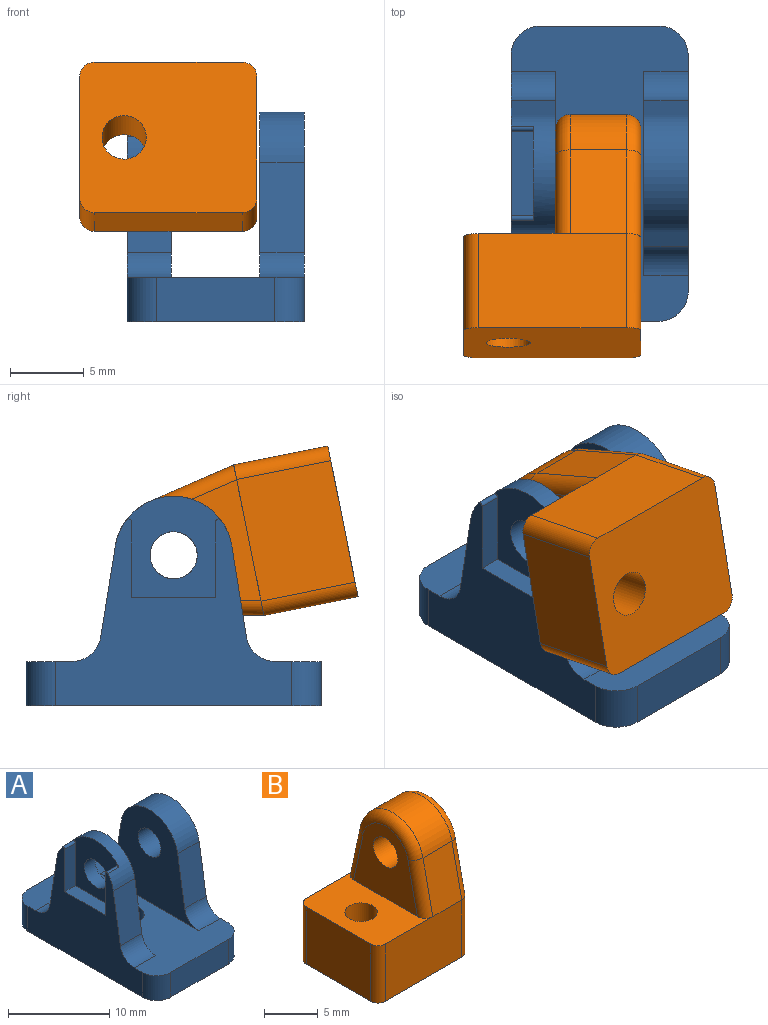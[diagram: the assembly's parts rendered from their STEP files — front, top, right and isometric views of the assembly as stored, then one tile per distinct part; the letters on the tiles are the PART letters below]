
ASSEMBLY  parts=2 mates=1
PART A: 31 faces, bbox 12x20x14.2 mm
  f0: cylinder r=4mm len=7.9mm, axis (-1,0,0), area 22.7mm2, adj f4,f14,f15,f16,f28,f29,f30
  f1: cylinder r=1.6mm len=3.2mm, axis (-1,0,0), area 15.1mm2, adj f16,f28
  f2: plane 16x14.2mm, normal (1,0,0), area 132.9mm2, adj f7,f8,f9,f10,f11,f12,f19,f20
  f3: plane 8x3mm, normal (0,1,0), area 24mm2, adj f7,f8,f21,f22
  f4: plane 16x12.67mm, normal (-1,0,0), area 103.9mm2, adj f0,f7,f8,f14,f15,f17,f18,f22
  f5: plane 8x3mm, normal (0,-1,0), area 24mm2, adj f7,f8,f23,f24
  f6: cylinder r=1.6mm len=3.2mm, axis (0,0,-1), area 30.2mm2, adj f7,f8
  f7: plane 20x12mm, normal (0,0,1), area 145.7mm2, adj f2,f3,f4,f5,f6,f13,f16,f17
  f8: plane 20x12mm, normal (0,0,-1), area 228.5mm2, adj f2,f3,f4,f5,f6,f21,f22,f23
  f9: cylinder r=4mm len=7.9mm, axis (1,0,0), area 33.9mm2, adj f2,f10,f12,f13
  f10: plane 6.15x3mm, normal (0,-0.99,0.16), area 18.7mm2, adj f2,f9,f13,f19
  f11: cylinder r=1.6mm len=3.2mm, axis (1,0,0), area 30.2mm2, adj f2,f13
  f12: plane 6.15x3mm, normal (0,0.99,0.16), area 18.7mm2, adj f2,f9,f13,f20
  f13: plane 13.81x11.2mm, normal (-1,0,0), area 84.9mm2, adj f7,f9,f10,f11,f12,f19,f20
  f14: plane 6.15x3mm, normal (0,0.99,0.16), area 18.7mm2, adj f0,f4,f16,f18
  f15: plane 6.15x3mm, normal (0,-0.99,0.16), area 18.7mm2, adj f0,f4,f16,f17
  f16: plane 13.81x11.2mm, normal (1,0,0), area 84.9mm2, adj f0,f1,f7,f14,f15,f17,f18
  f17: cylinder r=2mm len=3mm, axis (-1,0,0), area 8.5mm2, adj f4,f7,f15,f16
  f18: cylinder r=2mm len=3mm, axis (-1,0,0), area 8.5mm2, adj f4,f7,f14,f16
  f19: cylinder r=2mm len=3mm, axis (-1,0,0), area 8.5mm2, adj f2,f7,f10,f13
  f20: cylinder r=2mm len=3mm, axis (-1,0,0), area 8.5mm2, adj f2,f7,f12,f13
  f21: cylinder r=2mm len=3mm, axis (0,0,1), area 9.4mm2, adj f2,f3,f7,f8
  f22: cylinder r=2mm len=3mm, axis (0,0,-1), area 9.4mm2, adj f3,f4,f7,f8
  f23: cylinder r=2mm len=3mm, axis (0,0,1), area 9.4mm2, adj f4,f5,f7,f8
  f24: cylinder r=2mm len=3mm, axis (0,0,-1), area 9.4mm2, adj f2,f5,f7,f8
  f25: plane 5.12x1.5mm, normal (0,-1,0), area 7.7mm2, adj f4,f26,f28,f29
  f26: plane 5.7x1.5mm, normal (0,0,1), area 8.6mm2, adj f4,f25,f27,f28
  f27: plane 5.12x1.5mm, normal (0,1,0), area 7.7mm2, adj f4,f26,f28,f30
  f28: plane 6.85x6.42mm, normal (-1,0,0), area 29mm2, adj f0,f1,f25,f26,f27,f29,f30
  f29: cylinder r=0.2mm len=1.5mm, axis (-1,0,0), area 0.8mm2, adj f0,f4,f25,f28
  f30: cylinder r=0.2mm len=1.5mm, axis (-1,0,0), area 0.8mm2, adj f0,f4,f27,f28
PART B: 22 faces, bbox 12x10.4x16 mm
  f0: plane 14.7x8.4mm, normal (1,0,0), area 98.4mm2, adj f6,f9,f12,f13,f14,f15,f16
  f1: plane 10x6.5mm, normal (0,1,0), area 65mm2, adj f5,f6,f10,f12,f20
  f2: plane 8.4x6.5mm, normal (-1,0,0), area 54.6mm2, adj f5,f6,f20,f21
  f3: plane 10x6.5mm, normal (0,-1,0), area 65mm2, adj f5,f6,f8,f15,f21
  f4: cylinder r=1.5mm len=6.5mm, axis (0,0,-1), area 61.3mm2, adj f5,f6
  f5: plane 10.4x7.2mm, normal (0,0,1), area 57.4mm2, adj f1,f2,f3,f4,f11,f17,f19,f20
  f6: plane 12x10.4mm, normal (0,0,-1), area 116.9mm2, adj f0,f1,f2,f3,f4,f12,f15,f20
  f7: cylinder r=4mm len=7.82mm, axis (1,0,0), area 41.4mm2, adj f8,f10,f14,f18
  f8: plane 6.04x3.8mm, normal (0,-0.98,0.21), area 23.4mm2, adj f3,f7,f16,f19
  f9: cylinder r=1.6mm len=5.8mm, axis (1,0,0), area 58.3mm2, adj f0,f11
  f10: plane 6.04x3.8mm, normal (0,0.98,0.21), area 23.4mm2, adj f1,f7,f13,f17
  f11: plane 8.36x8.2mm, normal (-1,0,0), area 43.8mm2, adj f5,f9,f17,f18,f19
  f12: cylinder r=1mm len=6.5mm, axis (0,0,1), area 10.1mm2, adj f0,f1,f6,f13
  f13: cylinder r=1mm len=6.24mm, axis (0,-0.21,0.98), area 9.6mm2, adj f0,f10,f12,f14
  f14: torus R=3mm, axis (1,0,0), area 15.5mm2, adj f0,f7,f13,f16
  f15: cylinder r=1mm len=6.5mm, axis (0,0,-1), area 10.1mm2, adj f0,f3,f6,f16
  f16: cylinder r=1mm len=6.24mm, axis (0,-0.21,-0.98), area 9.6mm2, adj f0,f8,f14,f15
  f17: cylinder r=1mm len=6.24mm, axis (0,0.21,-0.98), area 9.6mm2, adj f5,f10,f11,f18
  f18: torus R=3mm, axis (1,0,0), area 15.5mm2, adj f7,f11,f17,f19
  f19: cylinder r=1mm len=6.24mm, axis (0,0.21,0.98), area 9.6mm2, adj f5,f8,f11,f18
  f20: cylinder r=1mm len=6.5mm, axis (0,0,-1), area 10.2mm2, adj f1,f2,f5,f6
  f21: cylinder r=1mm len=6.5mm, axis (0,0,1), area 10.2mm2, adj f2,f3,f5,f6
PLACE A t=(6.01,1.61,-1.19)mm fixed
PLACE B rot(axis=(-1,0,0),101.3deg) t=(2.81,-9.86,11.31)mm
MATE revolute A.f1 <-> B.f9  axis (1,0,0) through (3.01,1.61,9.01)mm
